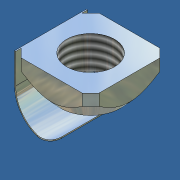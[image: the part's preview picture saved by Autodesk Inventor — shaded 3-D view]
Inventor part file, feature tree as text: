
AUTODESK INVENTOR PART (.ipt)
format: ipt  version: 2012 (Build 160160000, 160)  size: 163,328 bytes
history: native  units: mm
features: sketch x3, extrude x2, plane x1, revolve x1, thread x1, fillet x1
ambient origin geometry x8: Origin, YZ Plane, XZ Plane, XY Plane, X Axis, Y Axis, Z Axis, Center Point
bodies: Solid1 (feature_tree)
feature tree (9):
  extrude  "Extrusion1"  Depth=2.0mm
  plane  "Work Plane1"
  revolve  "Revolution1"  [1 undecoded]
  thread  "Thread1"  [1 undecoded]
  fillet  "Fillet2"  Radius=10.0mm
  sketch  "Sketch2"  dims[d3=45.0deg d4=2.0mm]
  sketch  "Sketch4"  dims[d5=5.5mm d6=0.0mm d10=5.0mm d12=90.0deg d13=10.0mm d14=0.0mm]
  sketch  "Sketch6"  dims[d15=2.0mm d21=10.8mm d22=0.2mm d23=0.2mm d24=5.374337mm d25=5.0mm d27=0.0mm d28=12.0mm d29=2.0mm]
  extrude  "Extrusion3"  Depth=2.0mm
note: 2 required parameter values undecoded (feature->parameter linkage not recoverable at this tier; creation-order binding heuristic only, values carry confidence <= 0.55)